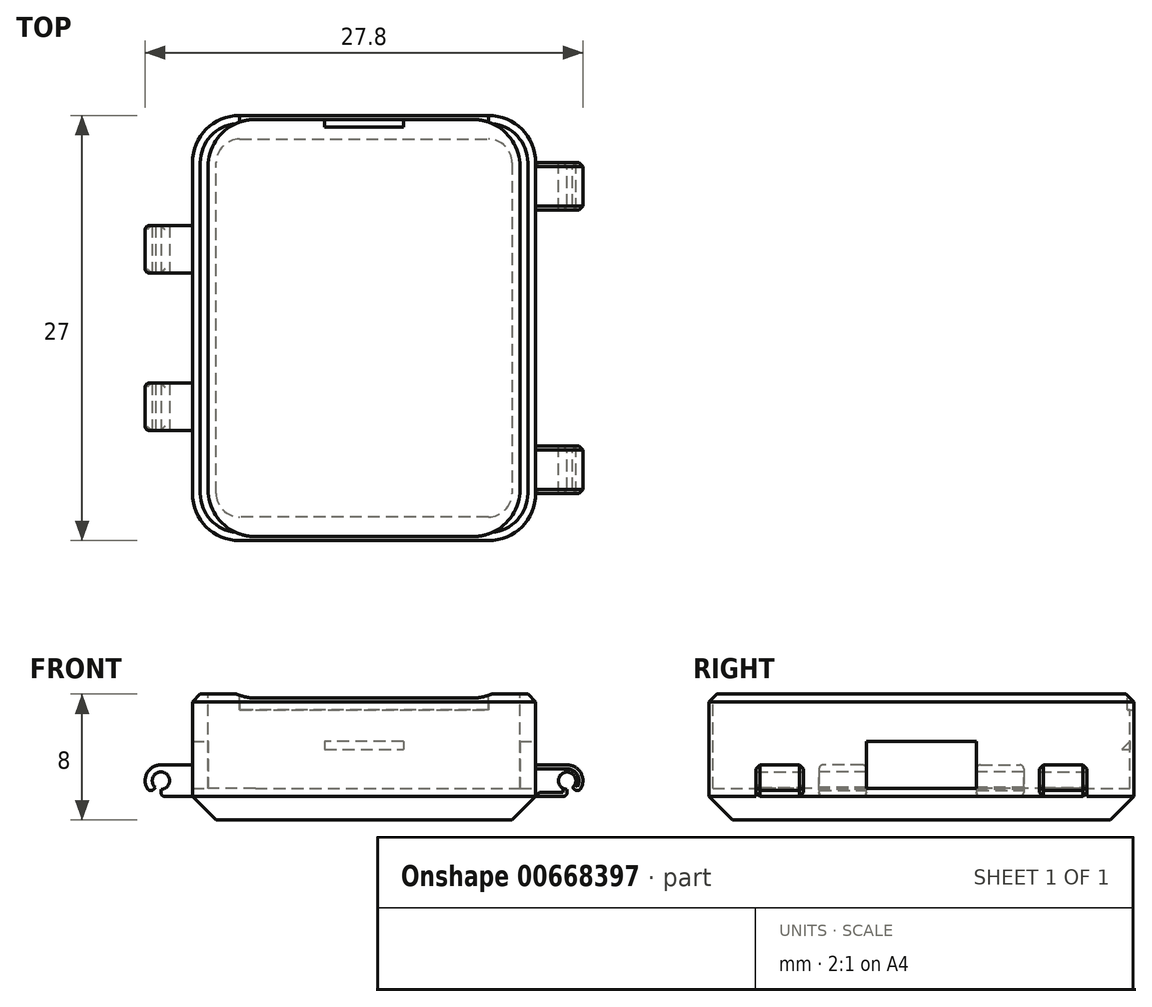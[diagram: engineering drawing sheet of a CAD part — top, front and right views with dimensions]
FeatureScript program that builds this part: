
annotation { "Feature Type Name" : "Feature", "Feature Type Description" : "" }
export const myFeature = defineFeature(function(context is Context, id is Id, definition is map)
    precondition{}
    {
        {
            var Q0;
            Q0=qCreatedBy(makeId("Top.planeOp"),FACE);
            var sketch = newSketch(context, id + "F0", { "sketchPlane" : qUnion([Q0])});
            skLineSegment(sketch, "E0.bottom", {"start": v(3, 0) * mm, "end": v(18.8, 0) * mm});
            skLineSegment(sketch, "E0.top", {"start": v(3, 27) * mm, "end": v(18.8, 27) * mm});
            skLineSegment(sketch, "E0.left", {"start": v(0, 3) * mm, "end": v(0, 24) * mm});
            skLineSegment(sketch, "E0.right", {"start": v(21.8, 3) * mm, "end": v(21.8, 24) * mm});
            skPoint(sketch, "E1.visualSharp", {"position": v(0, 27) * mm});
            skArc(sketch, "E1.filletArc", {"start": v(3, 27) * mm, "mid": v(0.88, 26.12) * mm, "end": v(0, 24) * mm});
            skPoint(sketch, "E2.visualSharp", {"position": v(21.8, 27) * mm});
            skArc(sketch, "E2.filletArc", {"start": v(21.8, 24) * mm, "mid": v(20.92, 26.12) * mm, "end": v(18.8, 27) * mm});
            skPoint(sketch, "E3.visualSharp", {"position": v(21.8, 0) * mm});
            skArc(sketch, "E3.filletArc", {"start": v(18.8, 0) * mm, "mid": v(20.92, 0.88) * mm, "end": v(21.8, 3) * mm});
            skPoint(sketch, "E4.visualSharp", {"position": v(0, 0) * mm});
            skArc(sketch, "E4.filletArc", {"start": v(0, 3) * mm, "mid": v(0.88, 0.88) * mm, "end": v(3, 0) * mm});
            skSolve(sketch);
        }
        {
            var Q0;
            Q0 = qSketchRegion(id + "F0", true);
            extrude(context, id + "F1", {"entities" : qUnion([Q0]), "depth" : 8 * mm, "offsetDistance" : 25 * mm});
        }
        {
            var Q0;
            Q0=makeQuery(id+"F1.opExtrude","CAP_FACE",FACE,{"disambiguationData":[OSD([sQuery(id+"F0.wireOp",EDGE,"E0.bottom"),sQuery(id+"F0.wireOp",EDGE,"E0.top"),sQuery(id+"F0.wireOp",EDGE,"E0.left"),sQuery(id+"F0.wireOp",EDGE,"E0.right"),sQuery(id+"F0.wireOp",EDGE,"E1.filletArc"),sQuery(id+"F0.wireOp",EDGE,"E2.filletArc"),sQuery(id+"F0.wireOp",EDGE,"E3.filletArc"),sQuery(id+"F0.wireOp",EDGE,"E4.filletArc")])],"isStart":false});
            var sketch = newSketch(context, id + "F2", { "sketchPlane" : qUnion([Q0])});
            skLineSegment(sketch, "E5.bottom", {"start": v(4, 26.75) * mm, "end": v(17.8, 26.75) * mm});
            skLineSegment(sketch, "E5.top", {"start": v(4, 0.25) * mm, "end": v(17.8, 0.25) * mm});
            skLineSegment(sketch, "E5.left", {"start": v(1, 23.75) * mm, "end": v(1, 3.25) * mm});
            skLineSegment(sketch, "E5.right", {"start": v(20.8, 23.75) * mm, "end": v(20.8, 3.25) * mm});
            skPoint(sketch, "E6.visualSharp", {"position": v(1, 0.25) * mm});
            skArc(sketch, "E6.filletArc", {"start": v(1, 3.25) * mm, "mid": v(1.88, 1.13) * mm, "end": v(4, 0.25) * mm});
            skPoint(sketch, "E7.visualSharp", {"position": v(20.8, 0.25) * mm});
            skArc(sketch, "E7.filletArc", {"start": v(17.8, 0.25) * mm, "mid": v(19.92, 1.13) * mm, "end": v(20.8, 3.25) * mm});
            skPoint(sketch, "E8.visualSharp", {"position": v(20.8, 26.75) * mm});
            skArc(sketch, "E8.filletArc", {"start": v(20.8, 23.75) * mm, "mid": v(19.92, 25.87) * mm, "end": v(17.8, 26.75) * mm});
            skPoint(sketch, "E9.visualSharp", {"position": v(1, 26.75) * mm});
            skArc(sketch, "E9.filletArc", {"start": v(4, 26.75) * mm, "mid": v(1.88, 25.87) * mm, "end": v(1, 23.75) * mm});
            skSolve(sketch);
        }
        {
            var Q0;
            Q0 = qSketchRegion(id + "F2", true);
            extrude(context, id + "F3", {"entities" : qUnion([Q0]), "operationType" : NewBodyOperationType.REMOVE, "oppositeDirection" : true, "depth" : 6 * mm, "offsetDistance" : 25 * mm});
        }
        {
            var Q0;
            Q0=makeQuery(id+"F1.opExtrude","SWEPT_FACE",FACE,{"disambiguationData":[OSD([sQuery(id+"F0.wireOp",EDGE,"E0.right")])]});
            var sketch = newSketch(context, id + "F4", { "sketchPlane" : qUnion([Q0])});
            skLineSegment(sketch, "E10.bottom", {"start": v(10, 2) * mm, "end": v(17, 2) * mm});
            skLineSegment(sketch, "E10.top", {"start": v(10, 5) * mm, "end": v(17, 5) * mm});
            skLineSegment(sketch, "E10.left", {"start": v(10, 2) * mm, "end": v(10, 5) * mm});
            skLineSegment(sketch, "E10.right", {"start": v(17, 2) * mm, "end": v(17, 5) * mm});
            skSolve(sketch);
        }
        {
            var Q0;
            Q0 = qSketchRegion(id + "F4", true);
            extrude(context, id + "F5", {"entities" : qUnion([Q0]), "operationType" : NewBodyOperationType.REMOVE, "oppositeDirection" : true, "depth" : 21.8 * mm, "offsetDistance" : 25 * mm});
        }
        {
            var Q0;
            Q0=makeQuery(id+"F1.opExtrude","SWEPT_FACE",FACE,{"disambiguationData":[OSD([sQuery(id+"F0.wireOp",EDGE,"E0.top")])]});
            var sketch = newSketch(context, id + "F6", { "sketchPlane" : qUnion([Q0])});
            skLineSegment(sketch, "E11.bottom", {"start": v(-18.8, 8) * mm, "end": v(-3, 8) * mm});
            skLineSegment(sketch, "E11.top", {"start": v(-18.8, 7) * mm, "end": v(-3, 7) * mm});
            skLineSegment(sketch, "E11.left", {"start": v(-18.8, 8) * mm, "end": v(-18.8, 7) * mm});
            skLineSegment(sketch, "E11.right", {"start": v(-3, 8) * mm, "end": v(-3, 7) * mm});
            skSolve(sketch);
        }
        {
            var Q0;
            Q0 = qSketchRegion(id + "F6", true);
            extrude(context, id + "F7", {"entities" : qUnion([Q0]), "operationType" : NewBodyOperationType.REMOVE, "oppositeDirection" : true, "depth" : 3 * mm, "offsetDistance" : 25 * mm});
        }
        {
            var Q0;
            Q0=makeQuery(id+"F1.opExtrude","CAP_EDGE",EDGE,{"disambiguationData":[OSD([sQuery(id+"F0.wireOp",EDGE,"E0.left")])],"isStart":true});
            chamfer(context, id + "F8", {"entities" : qUnion([Q0]), "width" : 1.5 * mm, "tangentPropagation" : true});
        }
        {
            var Q0;
            Q0=makeQuery(id+"F1.opExtrude","CAP_EDGE",EDGE,{"disambiguationData":[OSD([sQuery(id+"F0.wireOp",EDGE,"E0.left")])],"isStart":false});
            var Q1;
            Q1=makeQuery(id+"F1.opExtrude","CAP_EDGE",EDGE,{"disambiguationData":[OSD([sQuery(id+"F0.wireOp",EDGE,"E0.right")])],"isStart":false});
            chamfer(context, id + "F9", {"entities" : qUnion([Q0, Q1]), "width" : .5 * mm, "tangentPropagation" : true});
        }
        {
            var Q0;
            Q0=makeQuery(id+"F3.boolean.opBoolean","COPY",FACE,{"derivedFrom":makeQuery(id+"F3.opExtrude","SWEPT_FACE",FACE,{"disambiguationData":[OSD([sQuery(id+"F2.wireOp",EDGE,"E5.bottom")])]})});
            var sketch = newSketch(context, id + "F10", { "sketchPlane" : qUnion([Q0])});
            skLineSegment(sketch, "E12.bottom", {"start": v(8.4, 6.5) * mm, "end": v(13.4, 6.5) * mm});
            skLineSegment(sketch, "E12.top", {"start": v(8.4, 4.5) * mm, "end": v(13.4, 4.5) * mm});
            skLineSegment(sketch, "E12.left", {"start": v(8.4, 6.5) * mm, "end": v(8.4, 4.5) * mm});
            skLineSegment(sketch, "E12.right", {"start": v(13.4, 6.5) * mm, "end": v(13.4, 4.5) * mm});
            skSolve(sketch);
        }
        {
            var Q0;
            Q0 = qSketchRegion(id + "F10", true);
            extrude(context, id + "F11", {"entities" : qUnion([Q0]), "operationType" : NewBodyOperationType.ADD, "depth" : .5 * mm, "offsetDistance" : 25 * mm});
        }
        {
            var Q0;
            Q0=makeQuery(id+"F11.opExtrude","CAP_EDGE",EDGE,{"disambiguationData":[OSD([sQuery(id+"F10.wireOp",EDGE,"E12.bottom")])],"isStart":false});
            chamfer(context, id + "F12", {"entities" : qUnion([Q0]), "width" : 2 * mm, "tangentPropagation" : true});
        }
        {
            var Q0;
            Q0=makeQuery(id+"F1.opExtrude","SWEPT_FACE",FACE,{"disambiguationData":[OSD([sQuery(id+"F0.wireOp",EDGE,"E0.right")])]});
            var sketch = newSketch(context, id + "F13", { "sketchPlane" : qUnion([Q0])});
            skLineSegment(sketch, "E13.bottom", {"start": v(3, 3.5) * mm, "end": v(6, 3.5) * mm});
            skLineSegment(sketch, "E13.top", {"start": v(3, 1.5) * mm, "end": v(6, 1.5) * mm});
            skLineSegment(sketch, "E13.left", {"start": v(3, 3.5) * mm, "end": v(3, 1.5) * mm});
            skLineSegment(sketch, "E13.right", {"start": v(6, 3.5) * mm, "end": v(6, 1.5) * mm});
            skLineSegment(sketch, "E14.bottom", {"start": v(24, 3.5) * mm, "end": v(21, 3.5) * mm});
            skLineSegment(sketch, "E14.top", {"start": v(24, 1.5) * mm, "end": v(21, 1.5) * mm});
            skLineSegment(sketch, "E14.left", {"start": v(24, 3.5) * mm, "end": v(24, 1.5) * mm});
            skLineSegment(sketch, "E14.right", {"start": v(21, 3.5) * mm, "end": v(21, 1.5) * mm});
            skSolve(sketch);
        }
        {
            var Q0;
            Q0 = qSketchRegion(id + "F13", true);
            extrude(context, id + "F14", {"entities" : qUnion([Q0]), "operationType" : NewBodyOperationType.ADD, "depth" : 2 * mm, "offsetDistance" : 25 * mm});
        }
        {
            var Q0;
            Q0=makeQuery(id+"F14.opExtrude","CAP_FACE",FACE,{"disambiguationData":[OSD([sQuery(id+"F13.wireOp",EDGE,"E13.bottom"),sQuery(id+"F13.wireOp",EDGE,"E13.top"),sQuery(id+"F13.wireOp",EDGE,"E13.left"),sQuery(id+"F13.wireOp",EDGE,"E13.right")])],"isStart":false});
            var sketch = newSketch(context, id + "F15", { "sketchPlane" : qUnion([Q0])});
            skLineSegment(sketch, "E15.bottom", {"start": v(3, 3.5) * mm, "end": v(6, 3.5) * mm});
            skLineSegment(sketch, "E15.top", {"start": v(3, 2.5) * mm, "end": v(6, 2.5) * mm});
            skLineSegment(sketch, "E15.left", {"start": v(3, 3.5) * mm, "end": v(3, 2.5) * mm});
            skLineSegment(sketch, "E15.right", {"start": v(6, 3.5) * mm, "end": v(6, 2.5) * mm});
            skSolve(sketch);
        }
        {
            var Q0;
            Q0 = qSketchRegion(id + "F15", true);
            var Q1;
            Q1=sQuery(id+"F15.wireOp",EDGE,"E15.top");
            revolve(context, id + "F16", {"operationType" : NewBodyOperationType.ADD, "entities" : qUnion([Q0]), "axis" : qUnion([Q1]), "revolveType" : RevolveType.TWO_DIRECTIONS, "angle" : 140 * degree, "angleBack" : 246.32 * degree});
        }
        {
            var Q0;
            Q0=makeQuery(id+"F14.opExtrude","CAP_FACE",FACE,{"disambiguationData":[OSD([sQuery(id+"F13.wireOp",EDGE,"E14.bottom"),sQuery(id+"F13.wireOp",EDGE,"E14.top"),sQuery(id+"F13.wireOp",EDGE,"E14.left"),sQuery(id+"F13.wireOp",EDGE,"E14.right")])],"isStart":false});
            var sketch = newSketch(context, id + "F17", { "sketchPlane" : qUnion([Q0])});
            skLineSegment(sketch, "E16.bottom", {"start": v(21, 3.5) * mm, "end": v(24, 3.5) * mm});
            skLineSegment(sketch, "E16.top", {"start": v(21, 2.5) * mm, "end": v(24, 2.5) * mm});
            skLineSegment(sketch, "E16.left", {"start": v(21, 3.5) * mm, "end": v(21, 2.5) * mm});
            skLineSegment(sketch, "E16.right", {"start": v(24, 3.5) * mm, "end": v(24, 2.5) * mm});
            skSolve(sketch);
        }
        {
            var Q0;
            Q0 = qSketchRegion(id + "F17", true);
            var Q1;
            Q1=sQuery(id+"F17.wireOp",EDGE,"E16.top");
            revolve(context, id + "F18", {"operationType" : NewBodyOperationType.ADD, "entities" : qUnion([Q0]), "axis" : qUnion([Q1]), "revolveType" : RevolveType.TWO_DIRECTIONS, "angle" : 140 * degree, "angleBack" : 330 * degree});
        }
        {
            var Q0;
            Q0=makeQuery(id+"F18.boolean.opBoolean","MERGE",FACE,{"derivedFrom":[makeQuery(id+"F14.opExtrude","SWEPT_FACE",FACE,{"disambiguationData":[OSD([sQuery(id+"F13.wireOp",EDGE,"E14.left")])]}),makeQuery(id+"F18.opRevolve","SWEPT_FACE",FACE,{"disambiguationData":[OSD([sQuery(id+"F17.wireOp",EDGE,"E16.right")])]})]});
            var sketch = newSketch(context, id + "F19", { "sketchPlane" : qUnion([Q0])});
            skCircle(sketch, "E17", {"center": v(-23.8, 2.5) * mm, "radius": 0.55 * mm});
            skSolve(sketch);
        }
        {
            var Q0;
            Q0 = qSketchRegion(id + "F19", true);
            extrude(context, id + "F20", {"entities" : qUnion([Q0]), "operationType" : NewBodyOperationType.REMOVE, "endBound" : BoundingType.THROUGH_ALL, "oppositeDirection" : true, "depth" : 25 * mm, "offsetDistance" : 25 * mm});
        }
        {
            var Q0;
            Q0=makeQuery(id+"F14.opExtrude","CAP_EDGE",EDGE,{"disambiguationData":[OSD([sQuery(id+"F13.wireOp",EDGE,"E13.top")])],"isStart":false});
            var Q1;
            Q1=makeQuery(id+"F14.opExtrude","CAP_EDGE",EDGE,{"disambiguationData":[OSD([sQuery(id+"F13.wireOp",EDGE,"E14.top")])],"isStart":false});
            fillet(context, id + "F21", {"entities" : qUnion([Q0, Q1]), "radius" : 0.25 * mm, "tangentPropagation" : true, "allowEdgeOverflow" : false});
        }
        {
            var Q0;
            Q0=makeQuery(id+"F16.opRevolve","CAP_EDGE",EDGE,{"disambiguationData":[OSD([sQuery(id+"F15.wireOp",EDGE,"E15.bottom")])],"isStart":false});
            var Q1;
            Q1=makeQuery(id+"F18.opRevolve","CAP_EDGE",EDGE,{"disambiguationData":[OSD([sQuery(id+"F17.wireOp",EDGE,"E16.bottom")])],"isStart":false});
            fillet(context, id + "F22", {"entities" : qUnion([Q0, Q1]), "radius" : 0.25 * mm, "tangentPropagation" : true, "allowEdgeOverflow" : false});
        }
        {
            var Q0;
            Q0=makeQuery(id+"F14.opExtrude","SWEPT_EDGE",EDGE,{"disambiguationData":[OSD([sQuery(id+"F0.wireOp",EDGE,"E0.right"),sQuery(id+"F13.wireOp",EDGE,"E14.top"),sQuery(id+"F13.wireOp",EDGE,"E14.right")])]});
            var Q1;
            Q1=makeQuery(id+"F14.opExtrude","SWEPT_EDGE",EDGE,{"disambiguationData":[OSD([sQuery(id+"F0.wireOp",EDGE,"E0.right"),sQuery(id+"F13.wireOp",EDGE,"E13.top"),sQuery(id+"F13.wireOp",EDGE,"E13.right")])]});
            var Q2;
            Q2=makeQuery(id+"F14.opExtrude","SWEPT_EDGE",EDGE,{"disambiguationData":[OSD([sQuery(id+"F13.wireOp",EDGE,"E13.top"),sQuery(id+"F13.wireOp",EDGE,"E13.left")])]});
            var Q3;
            Q3=makeQuery(id+"F14.opExtrude","SWEPT_EDGE",EDGE,{"disambiguationData":[OSD([sQuery(id+"F13.wireOp",EDGE,"E14.top"),sQuery(id+"F13.wireOp",EDGE,"E14.left")])]});
            chamfer(context, id + "F23", {"entities" : qUnion([Q0, Q1, Q2, Q3]), "width" : .25 * mm, "tangentPropagation" : true});
        }
        {
            var Q0;
            Q0=makeQuery(id+"F14.opExtrude","SWEPT_EDGE",EDGE,{"disambiguationData":[OSD([sQuery(id+"F13.wireOp",EDGE,"E14.bottom"),sQuery(id+"F13.wireOp",EDGE,"E14.right")])]});
            var Q1;
            Q1=makeQuery(id+"F18.opRevolve","SWEPT_EDGE",EDGE,{"disambiguationData":[OSD([sQuery(id+"F17.wireOp",EDGE,"E16.bottom"),sQuery(id+"F17.wireOp",EDGE,"E16.left")])]});
            var Q2;
            Q2=makeQuery(id+"F14.opExtrude","SWEPT_EDGE",EDGE,{"disambiguationData":[OSD([sQuery(id+"F0.wireOp",EDGE,"E0.right"),sQuery(id+"F0.wireOp",EDGE,"E2.filletArc"),sQuery(id+"F13.wireOp",EDGE,"E14.bottom"),sQuery(id+"F13.wireOp",EDGE,"E14.left")])]});
            var Q3;
            Q3=makeQuery(id+"F14.opExtrude","SWEPT_EDGE",EDGE,{"disambiguationData":[OSD([sQuery(id+"F13.wireOp",EDGE,"E13.bottom"),sQuery(id+"F13.wireOp",EDGE,"E13.right")])]});
            var Q4;
            Q4=makeQuery(id+"F16.opRevolve","SWEPT_EDGE",EDGE,{"disambiguationData":[OSD([sQuery(id+"F15.wireOp",EDGE,"E15.bottom"),sQuery(id+"F15.wireOp",EDGE,"E15.left")])]});
            var Q5;
            Q5=makeQuery(id+"F14.opExtrude","SWEPT_EDGE",EDGE,{"disambiguationData":[OSD([sQuery(id+"F0.wireOp",EDGE,"E0.right"),sQuery(id+"F0.wireOp",EDGE,"E3.filletArc"),sQuery(id+"F13.wireOp",EDGE,"E13.bottom"),sQuery(id+"F13.wireOp",EDGE,"E13.left")])]});
            var Q6;
            Q6=makeQuery(id+"F16.opRevolve","SWEPT_EDGE",EDGE,{"disambiguationData":[OSD([sQuery(id+"F15.wireOp",EDGE,"E15.bottom"),sQuery(id+"F15.wireOp",EDGE,"E15.right")])]});
            var Q7;
            Q7=makeQuery(id+"F18.opRevolve","SWEPT_EDGE",EDGE,{"disambiguationData":[OSD([sQuery(id+"F17.wireOp",EDGE,"E16.bottom"),sQuery(id+"F17.wireOp",EDGE,"E16.right")])]});
            chamfer(context, id + "F24", {"entities" : qUnion([Q0, Q1, Q2, Q3, Q4, Q5, Q6, Q7]), "width" : 0.25 * mm, "tangentPropagation" : true});
        }
        {
            var Q0;
            Q0=makeQuery(id+"F1.opExtrude","SWEPT_FACE",FACE,{"disambiguationData":[OSD([sQuery(id+"F0.wireOp",EDGE,"E0.left")])]});
            var sketch = newSketch(context, id + "F25", { "sketchPlane" : qUnion([Q0])});
            skLineSegment(sketch, "E18.bottom", {"start": v(-17, 3.5) * mm, "end": v(-20, 3.5) * mm});
            skLineSegment(sketch, "E18.top", {"start": v(-17, 1.5) * mm, "end": v(-20, 1.5) * mm});
            skLineSegment(sketch, "E18.left", {"start": v(-17, 3.5) * mm, "end": v(-17, 1.5) * mm});
            skLineSegment(sketch, "E18.right", {"start": v(-20, 3.5) * mm, "end": v(-20, 1.5) * mm});
            skLineSegment(sketch, "E19.bottom", {"start": v(-10, 3.5) * mm, "end": v(-7, 3.5) * mm});
            skLineSegment(sketch, "E19.top", {"start": v(-10, 1.5) * mm, "end": v(-7, 1.5) * mm});
            skLineSegment(sketch, "E19.left", {"start": v(-10, 3.5) * mm, "end": v(-10, 1.5) * mm});
            skLineSegment(sketch, "E19.right", {"start": v(-7, 3.5) * mm, "end": v(-7, 1.5) * mm});
            skSolve(sketch);
        }
        {
            var Q0;
            Q0 = qSketchRegion(id + "F25", true);
            extrude(context, id + "F26", {"entities" : qUnion([Q0]), "operationType" : NewBodyOperationType.ADD, "depth" : 2 * mm, "offsetDistance" : 25 * mm});
        }
        {
            var Q0;
            Q0=makeQuery(id+"F26.opExtrude","CAP_FACE",FACE,{"disambiguationData":[OSD([sQuery(id+"F25.wireOp",EDGE,"E18.bottom"),sQuery(id+"F25.wireOp",EDGE,"E18.top"),sQuery(id+"F25.wireOp",EDGE,"E18.left"),sQuery(id+"F25.wireOp",EDGE,"E18.right")])],"isStart":false});
            var sketch = newSketch(context, id + "F27", { "sketchPlane" : qUnion([Q0])});
            skLineSegment(sketch, "E20.bottom", {"start": v(-20, 3.5) * mm, "end": v(-17, 3.5) * mm});
            skLineSegment(sketch, "E20.top", {"start": v(-20, 2.5) * mm, "end": v(-17, 2.5) * mm});
            skLineSegment(sketch, "E20.left", {"start": v(-20, 3.5) * mm, "end": v(-20, 2.5) * mm});
            skLineSegment(sketch, "E20.right", {"start": v(-17, 3.5) * mm, "end": v(-17, 2.5) * mm});
            skSolve(sketch);
        }
        {
            var Q0;
            Q0 = qSketchRegion(id + "F27", true);
            var Q1;
            Q1=sQuery(id+"F27.wireOp",EDGE,"E20.top");
            revolve(context, id + "F28", {"operationType" : NewBodyOperationType.ADD, "entities" : qUnion([Q0]), "axis" : qUnion([Q1]), "revolveType" : RevolveType.TWO_DIRECTIONS, "angle" : 140 * degree, "angleBack" : 330 * degree});
        }
        {
            var Q0;
            Q0=makeQuery(id+"F26.opExtrude","CAP_FACE",FACE,{"disambiguationData":[OSD([sQuery(id+"F25.wireOp",EDGE,"E19.bottom"),sQuery(id+"F25.wireOp",EDGE,"E19.top"),sQuery(id+"F25.wireOp",EDGE,"E19.left"),sQuery(id+"F25.wireOp",EDGE,"E19.right")])],"isStart":false});
            var sketch = newSketch(context, id + "F29", { "sketchPlane" : qUnion([Q0])});
            skLineSegment(sketch, "E21.bottom", {"start": v(-10, 3.5) * mm, "end": v(-7, 3.5) * mm});
            skLineSegment(sketch, "E21.top", {"start": v(-10, 2.5) * mm, "end": v(-7, 2.5) * mm});
            skLineSegment(sketch, "E21.left", {"start": v(-10, 3.5) * mm, "end": v(-10, 2.5) * mm});
            skLineSegment(sketch, "E21.right", {"start": v(-7, 3.5) * mm, "end": v(-7, 2.5) * mm});
            skSolve(sketch);
        }
        {
            var Q0;
            Q0 = qSketchRegion(id + "F29", true);
            var Q1;
            Q1=sQuery(id+"F29.wireOp",EDGE,"E21.top");
            revolve(context, id + "F30", {"operationType" : NewBodyOperationType.ADD, "entities" : qUnion([Q0]), "axis" : qUnion([Q1]), "revolveType" : RevolveType.TWO_DIRECTIONS, "angle" : 140 * degree, "angleBack" : 330 * degree});
        }
        {
            var Q0;
            Q0=makeQuery(id+"F30.boolean.opBoolean","MERGE",FACE,{"derivedFrom":[makeQuery(id+"F26.opExtrude","SWEPT_FACE",FACE,{"disambiguationData":[OSD([sQuery(id+"F25.wireOp",EDGE,"E19.right")])]}),makeQuery(id+"F30.opRevolve","SWEPT_FACE",FACE,{"disambiguationData":[OSD([sQuery(id+"F29.wireOp",EDGE,"E21.right")])]})]});
            var sketch = newSketch(context, id + "F31", { "sketchPlane" : qUnion([Q0])});
            skCircle(sketch, "E22", {"center": v(-2, 2.5) * mm, "radius": 0.55 * mm});
            skSolve(sketch);
        }
        {
            var Q0;
            Q0 = qSketchRegion(id + "F31", true);
            extrude(context, id + "F32", {"entities" : qUnion([Q0]), "operationType" : NewBodyOperationType.REMOVE, "endBound" : BoundingType.THROUGH_ALL, "oppositeDirection" : true, "depth" : 25 * mm, "offsetDistance" : 25 * mm});
        }
        {
            var Q0;
            Q0=makeQuery(id+"F28.opRevolve","CAP_EDGE",EDGE,{"disambiguationData":[OSD([sQuery(id+"F27.wireOp",EDGE,"E20.bottom")])],"isStart":false});
            var Q1;
            Q1=makeQuery(id+"F28.opRevolve","SWEPT_EDGE",EDGE,{"disambiguationData":[OSD([sQuery(id+"F27.wireOp",EDGE,"E20.bottom"),sQuery(id+"F27.wireOp",EDGE,"E20.right")])]});
            var Q2;
            Q2=makeQuery(id+"F26.opExtrude","CAP_EDGE",EDGE,{"disambiguationData":[OSD([sQuery(id+"F25.wireOp",EDGE,"E18.top")])],"isStart":false});
            var Q3;
            Q3=makeQuery(id+"F26.opExtrude","SWEPT_EDGE",EDGE,{"disambiguationData":[OSD([sQuery(id+"F0.wireOp",EDGE,"E0.left"),sQuery(id+"F25.wireOp",EDGE,"E18.top"),sQuery(id+"F25.wireOp",EDGE,"E18.right")])]});
            var Q4;
            Q4=makeQuery(id+"F26.opExtrude","SWEPT_EDGE",EDGE,{"disambiguationData":[OSD([sQuery(id+"F0.wireOp",EDGE,"E0.left"),sQuery(id+"F25.wireOp",EDGE,"E18.top"),sQuery(id+"F25.wireOp",EDGE,"E18.left")])]});
            var Q5;
            Q5=makeQuery(id+"F26.opExtrude","SWEPT_EDGE",EDGE,{"disambiguationData":[OSD([sQuery(id+"F25.wireOp",EDGE,"E18.bottom"),sQuery(id+"F25.wireOp",EDGE,"E18.right")])]});
            var Q6;
            Q6=makeQuery(id+"F26.opExtrude","SWEPT_EDGE",EDGE,{"disambiguationData":[OSD([sQuery(id+"F4.wireOp",EDGE,"E10.right"),sQuery(id+"F25.wireOp",EDGE,"E18.bottom"),sQuery(id+"F25.wireOp",EDGE,"E18.left")])]});
            var Q7;
            Q7=makeQuery(id+"F28.opRevolve","SWEPT_EDGE",EDGE,{"disambiguationData":[OSD([sQuery(id+"F27.wireOp",EDGE,"E20.bottom"),sQuery(id+"F27.wireOp",EDGE,"E20.left")])]});
            fillet(context, id + "F33", {"entities" : qUnion([Q0, Q1, Q2, Q3, Q4, Q5, Q6, Q7]), "radius" : 0.25 * mm, "tangentPropagation" : true, "allowEdgeOverflow" : false});
        }
        {
            var Q0;
            Q0=makeQuery(id+"F26.opExtrude","SWEPT_EDGE",EDGE,{"disambiguationData":[OSD([sQuery(id+"F0.wireOp",EDGE,"E0.left"),sQuery(id+"F25.wireOp",EDGE,"E19.top"),sQuery(id+"F25.wireOp",EDGE,"E19.left")])]});
            var Q1;
            Q1=makeQuery(id+"F30.opRevolve","SWEPT_EDGE",EDGE,{"disambiguationData":[OSD([sQuery(id+"F29.wireOp",EDGE,"E21.bottom"),sQuery(id+"F29.wireOp",EDGE,"E21.right")])]});
            var Q2;
            Q2=makeQuery(id+"F30.opRevolve","CAP_EDGE",EDGE,{"disambiguationData":[OSD([sQuery(id+"F29.wireOp",EDGE,"E21.bottom")])],"isStart":false});
            var Q3;
            Q3=makeQuery(id+"F26.opExtrude","SWEPT_EDGE",EDGE,{"disambiguationData":[OSD([sQuery(id+"F0.wireOp",EDGE,"E0.left"),sQuery(id+"F25.wireOp",EDGE,"E19.top"),sQuery(id+"F25.wireOp",EDGE,"E19.right")])]});
            var Q4;
            Q4=makeQuery(id+"F26.opExtrude","SWEPT_EDGE",EDGE,{"disambiguationData":[OSD([sQuery(id+"F25.wireOp",EDGE,"E19.bottom"),sQuery(id+"F25.wireOp",EDGE,"E19.right")])]});
            var Q5;
            Q5=makeQuery(id+"F26.opExtrude","SWEPT_EDGE",EDGE,{"disambiguationData":[OSD([sQuery(id+"F4.wireOp",EDGE,"E10.left"),sQuery(id+"F25.wireOp",EDGE,"E19.bottom"),sQuery(id+"F25.wireOp",EDGE,"E19.left")])]});
            var Q6;
            Q6=makeQuery(id+"F30.opRevolve","SWEPT_EDGE",EDGE,{"disambiguationData":[OSD([sQuery(id+"F29.wireOp",EDGE,"E21.bottom"),sQuery(id+"F29.wireOp",EDGE,"E21.left")])]});
            var Q7;
            Q7=makeQuery(id+"F26.opExtrude","CAP_EDGE",EDGE,{"disambiguationData":[OSD([sQuery(id+"F25.wireOp",EDGE,"E19.top")])],"isStart":false});
            fillet(context, id + "F34", {"entities" : qUnion([Q0, Q1, Q2, Q3, Q4, Q5, Q6, Q7]), "radius" : 0.25 * mm, "tangentPropagation" : true, "allowEdgeOverflow" : false});
        }
    });
